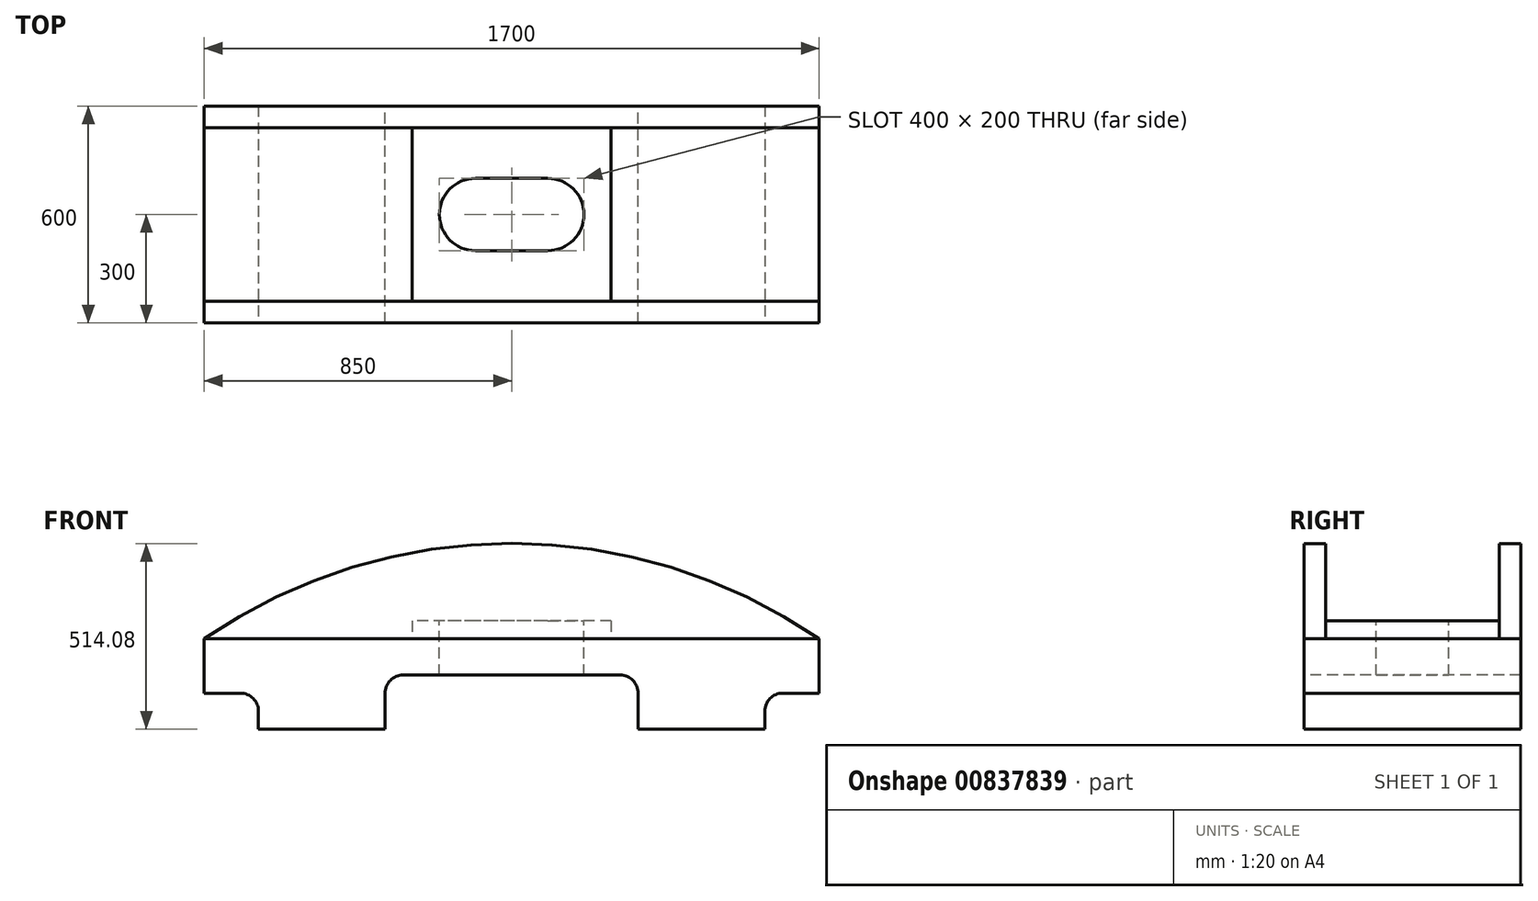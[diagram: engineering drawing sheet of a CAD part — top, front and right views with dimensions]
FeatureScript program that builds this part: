
annotation { "Feature Type Name" : "Feature", "Feature Type Description" : "" }
export const myFeature = defineFeature(function(context is Context, id is Id, definition is map)
    precondition{}
    {
        {
            var Q0;
            Q0=qCreatedBy(makeId("Front.planeOp"),FACE);
            var sketch = newSketch(context, id + "F0", { "sketchPlane" : qUnion([Q0])});
            skLineSegment(sketch, "E0.bottom", {"start": v(850, 125) * mm, "end": v(-850, 125) * mm});
            skLineSegment(sketch, "E0.top", {"start": v(850, -125) * mm, "end": v(-850, -125) * mm});
            skLineSegment(sketch, "E0.left", {"start": v(850, 125) * mm, "end": v(850, -125) * mm});
            skLineSegment(sketch, "E0.right", {"start": v(-850, 125) * mm, "end": v(-850, -125) * mm});
            skPoint(sketch, "E0.middle", {"position": v(0, 0) * mm});
            skSolve(sketch);
        }
        {
            var Q0;
            Q0 = qSketchRegion(id + "F0", true);
            extrude(context, id + "F1", {"entities" : qUnion([Q0]), "depth" : 600 * mm, "offsetDistance" : 25 * mm});
        }
        {
            var Q0;
            Q0=makeQuery(id+"F1.opExtrude","CAP_FACE",FACE,{"disambiguationData":[OSD([sQuery(id+"F0.wireOp",EDGE,"E0.bottom"),sQuery(id+"F0.wireOp",EDGE,"E0.top"),sQuery(id+"F0.wireOp",EDGE,"E0.left"),sQuery(id+"F0.wireOp",EDGE,"E0.right")])],"isStart":false});
            var sketch = newSketch(context, id + "F2", { "sketchPlane" : qUnion([Q0])});
            skLineSegment(sketch, "E1.bottom", {"start": v(-850, -125) * mm, "end": v(-700, -125) * mm});
            skLineSegment(sketch, "E1.top", {"start": v(-850, -25) * mm, "end": v(-750, -25) * mm});
            skLineSegment(sketch, "E1.left", {"start": v(-850, -125) * mm, "end": v(-850, -25) * mm});
            skLineSegment(sketch, "E1.right", {"start": v(-700, -125) * mm, "end": v(-700, -75) * mm});
            skLineSegment(sketch, "E2.bottom", {"start": v(850, -125) * mm, "end": v(700, -125) * mm});
            skLineSegment(sketch, "E2.top", {"start": v(850, -25) * mm, "end": v(750, -25) * mm});
            skLineSegment(sketch, "E2.left", {"start": v(850, -125) * mm, "end": v(850, -25) * mm});
            skLineSegment(sketch, "E2.right", {"start": v(700, -125) * mm, "end": v(700, -75) * mm});
            skPoint(sketch, "E3.visualSharp", {"position": v(-700, -25) * mm});
            skArc(sketch, "E3.filletArc", {"start": v(-700, -75) * mm, "mid": v(-714.64, -39.64) * mm, "end": v(-750, -25) * mm});
            skPoint(sketch, "E4.visualSharp", {"position": v(700, -25) * mm});
            skArc(sketch, "E4.filletArc", {"start": v(750, -25) * mm, "mid": v(714.64, -39.64) * mm, "end": v(700, -75) * mm});
            skSolve(sketch);
        }
        {
            var Q0;
            Q0 = qSketchRegion(id + "F2", true);
            extrude(context, id + "F3", {"entities" : qUnion([Q0]), "operationType" : NewBodyOperationType.REMOVE, "endBound" : BoundingType.THROUGH_ALL, "oppositeDirection" : true, "depth" : 25 * mm, "offsetDistance" : 25 * mm});
        }
        {
            var Q0;
            Q0=makeQuery(id+"F1.opExtrude","SWEPT_FACE",FACE,{"disambiguationData":[OSD([sQuery(id+"F0.wireOp",EDGE,"E0.bottom")])]});
            var sketch = newSketch(context, id + "F4", { "sketchPlane" : qUnion([Q0])});
            skLineSegment(sketch, "E5.bottom", {"start": v(275, -60) * mm, "end": v(-275, -60) * mm});
            skLineSegment(sketch, "E5.top", {"start": v(275, -540) * mm, "end": v(-275, -540) * mm});
            skLineSegment(sketch, "E5.left", {"start": v(275, -60) * mm, "end": v(275, -540) * mm});
            skLineSegment(sketch, "E5.right", {"start": v(-275, -60) * mm, "end": v(-275, -540) * mm});
            skPoint(sketch, "E5.middle", {"position": v(0, -300) * mm});
            skPoint(sketch, "E5.middle.positionSnap0", {"position": v(-850, -300) * mm});
            skPoint(sketch, "E5.centerSnap0", {"position": v(-850, -300) * mm});
            skSolve(sketch);
        }
        {
            var Q0;
            Q0 = qSketchRegion(id + "F4", true);
            extrude(context, id + "F5", {"entities" : qUnion([Q0]), "operationType" : NewBodyOperationType.ADD, "depth" : 50 * mm, "offsetDistance" : 25 * mm});
        }
        {
            var Q0;
            Q0=makeQuery(id+"F5.opExtrude","CAP_FACE",FACE,{"disambiguationData":[OSD([sQuery(id+"F4.wireOp",EDGE,"E5.bottom"),sQuery(id+"F4.wireOp",EDGE,"E5.top"),sQuery(id+"F4.wireOp",EDGE,"E5.left"),sQuery(id+"F4.wireOp",EDGE,"E5.right")])],"isStart":false});
            var sketch = newSketch(context, id + "F6", { "sketchPlane" : qUnion([Q0])});
            skPoint(sketch, "E6.middle.positionSnap0", {"position": v(-275, -300) * mm});
            skPoint(sketch, "E6.centerSnap0", {"position": v(-275, -300) * mm});
            skLineSegment(sketch, "E7.bottom", {"start": v(100, -200) * mm, "end": v(-100, -200) * mm});
            skLineSegment(sketch, "E7.top", {"start": v(100, -400) * mm, "end": v(-100, -400) * mm});
            skLineSegment(sketch, "E7.left", {"start": v(200, -300) * mm, "end": v(200, -300) * mm});
            skLineSegment(sketch, "E7.right", {"start": v(-200, -300) * mm, "end": v(-200, -300) * mm});
            skPoint(sketch, "E7.middle", {"position": v(0, -300) * mm});
            skPoint(sketch, "E8.visualSharp", {"position": v(200, -200) * mm});
            skArc(sketch, "E8.filletArc", {"start": v(200, -300) * mm, "mid": v(170.71, -229.29) * mm, "end": v(100, -200) * mm});
            skPoint(sketch, "E9.visualSharp", {"position": v(200, -400) * mm});
            skArc(sketch, "E9.filletArc", {"start": v(100, -400) * mm, "mid": v(170.71, -370.71) * mm, "end": v(200, -300) * mm});
            skPoint(sketch, "E10.visualSharp", {"position": v(-200, -400) * mm});
            skArc(sketch, "E10.filletArc", {"start": v(-200, -300) * mm, "mid": v(-170.71, -370.71) * mm, "end": v(-100, -400) * mm});
            skPoint(sketch, "E11.visualSharp", {"position": v(-200, -200) * mm});
            skArc(sketch, "E11.filletArc", {"start": v(-100, -200) * mm, "mid": v(-170.71, -229.29) * mm, "end": v(-200, -300) * mm});
            skSolve(sketch);
        }
        {
            var Q0;
            Q0 = qSketchRegion(id + "F6", true);
            extrude(context, id + "F7", {"entities" : qUnion([Q0]), "operationType" : NewBodyOperationType.REMOVE, "endBound" : BoundingType.THROUGH_ALL, "oppositeDirection" : true, "depth" : 25 * mm, "offsetDistance" : 25 * mm});
        }
        {
            var Q0;
            Q0=makeQuery(id+"F1.opExtrude","CAP_FACE",FACE,{"disambiguationData":[OSD([sQuery(id+"F0.wireOp",EDGE,"E0.bottom"),sQuery(id+"F0.wireOp",EDGE,"E0.top"),sQuery(id+"F0.wireOp",EDGE,"E0.left"),sQuery(id+"F0.wireOp",EDGE,"E0.right")])],"isStart":false});
            var sketch = newSketch(context, id + "F8", { "sketchPlane" : qUnion([Q0])});
            skArc(sketch, "E12", {"start": v(850, 125) * mm, "mid": v(0, 389.08) * mm, "end": v(-850, 125) * mm});
            skLineSegment(sketch, "E13", {"start": v(-850, 125) * mm, "end": v(850, 125) * mm});
            skSolve(sketch);
        }
        {
            var Q0;
            Q0 = qSketchRegion(id + "F8", true);
            extrude(context, id + "F9", {"entities" : qUnion([Q0]), "oppositeDirection" : true, "depth" : 60 * mm, "offsetDistance" : 25 * mm});
        }
        {
            var Q0;
            Q0=makeQuery(id+"F1.opExtrude","CAP_FACE",FACE,{"disambiguationData":[OSD([sQuery(id+"F0.wireOp",EDGE,"E0.bottom"),sQuery(id+"F0.wireOp",EDGE,"E0.top"),sQuery(id+"F0.wireOp",EDGE,"E0.left"),sQuery(id+"F0.wireOp",EDGE,"E0.right")])],"isStart":true});
            var sketch = newSketch(context, id + "F10", { "sketchPlane" : qUnion([Q0])});
            skArc(sketch, "E14", {"start": v(850, 125) * mm, "mid": v(0, 389.08) * mm, "end": v(-850, 125) * mm});
            skLineSegment(sketch, "E15", {"start": v(-850, 125) * mm, "end": v(850, 125) * mm});
            skSolve(sketch);
        }
        {
            var Q0;
            Q0 = qSketchRegion(id + "F10", true);
            extrude(context, id + "F11", {"entities" : qUnion([Q0]), "oppositeDirection" : true, "depth" : 60 * mm, "offsetDistance" : 25 * mm});
        }
        {
            var Q0;
            Q0=makeQuery(id+"F1.opExtrude","CAP_FACE",FACE,{"disambiguationData":[OSD([sQuery(id+"F0.wireOp",EDGE,"E0.bottom"),sQuery(id+"F0.wireOp",EDGE,"E0.top"),sQuery(id+"F0.wireOp",EDGE,"E0.left"),sQuery(id+"F0.wireOp",EDGE,"E0.right")])],"isStart":false});
            var sketch = newSketch(context, id + "F12", { "sketchPlane" : qUnion([Q0])});
            skLineSegment(sketch, "E16.bottom", {"start": v(300, 25) * mm, "end": v(-300, 25) * mm});
            skLineSegment(sketch, "E16.top", {"start": v(350, -275) * mm, "end": v(-350, -275) * mm});
            skLineSegment(sketch, "E16.left", {"start": v(350, -25) * mm, "end": v(350, -275) * mm});
            skLineSegment(sketch, "E16.right", {"start": v(-350, -25) * mm, "end": v(-350, -275) * mm});
            skPoint(sketch, "E16.middle", {"position": v(0, -125) * mm});
            skPoint(sketch, "E17.visualSharp", {"position": v(-350, 25) * mm});
            skArc(sketch, "E17.filletArc", {"start": v(-300, 25) * mm, "mid": v(-335.36, 10.36) * mm, "end": v(-350, -25) * mm});
            skPoint(sketch, "E18.visualSharp", {"position": v(350, 25) * mm});
            skArc(sketch, "E18.filletArc", {"start": v(350, -25) * mm, "mid": v(335.36, 10.36) * mm, "end": v(300, 25) * mm});
            skSolve(sketch);
        }
        {
            var Q0;
            Q0 = qSketchRegion(id + "F12", true);
            extrude(context, id + "F13", {"entities" : qUnion([Q0]), "operationType" : NewBodyOperationType.REMOVE, "endBound" : BoundingType.THROUGH_ALL, "oppositeDirection" : true, "depth" : 25 * mm, "offsetDistance" : 25 * mm});
        }
    });
